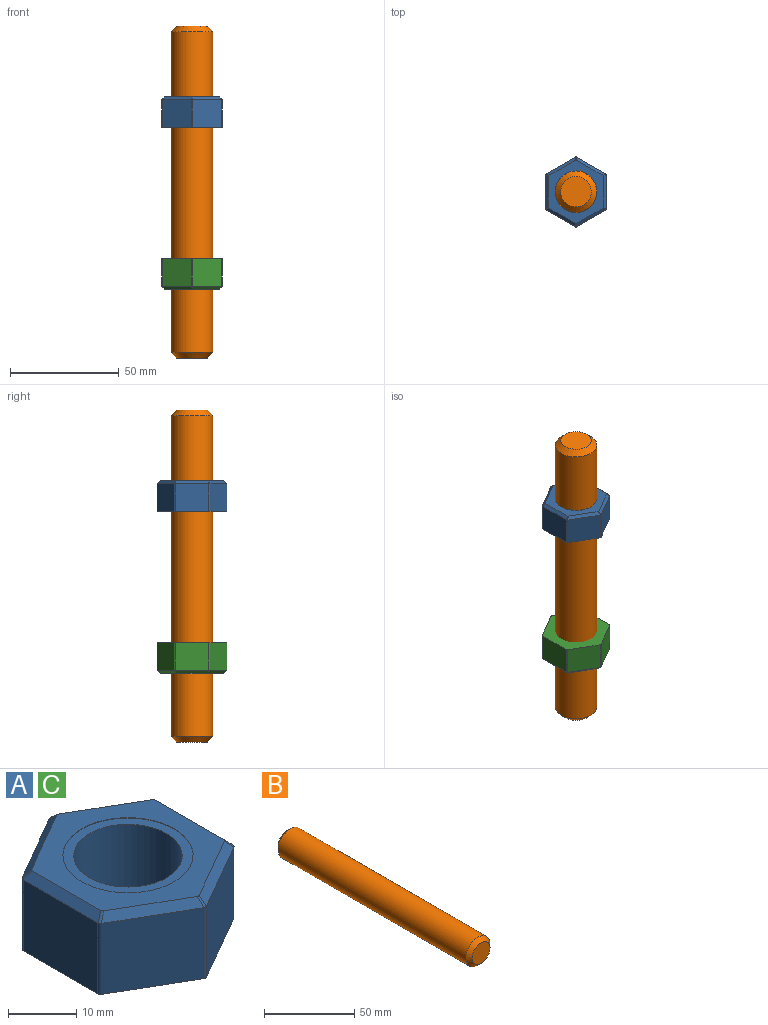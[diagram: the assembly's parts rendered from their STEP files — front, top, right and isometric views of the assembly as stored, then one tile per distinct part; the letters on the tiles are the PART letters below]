
ASSEMBLY  parts=3 mates=1
PART A: 29 faces, bbox 27.9x32.1x14 mm
  f0: plane 19.05x19.05mm, normal (0,0,1), area 87.1mm2, adj f2,f9
  f1: plane 32.05x27.93mm, normal (0,0,-1), area 477.5mm2, adj f2,f3,f4,f5,f6,f7,f8,f18
  f2: cylinder r=7.94mm len=15.88mm, axis (0,0,-1), area 692.8mm2, adj f0,f1
  f3: plane 15.39x12.7mm, normal (1,0,0), area 195.5mm2, adj f1,f14,f18,f26
  f4: plane 13.33x12.7mm, normal (0.5,-0.87,0), area 195.5mm2, adj f1,f12,f18,f20
  f5: plane 13.33x12.7mm, normal (-0.5,-0.87,0), area 195.5mm2, adj f1,f11,f20,f22
  f6: plane 15.39x12.7mm, normal (-1,0,0), area 195.5mm2, adj f1,f13,f22,f24
  f7: plane 13.33x12.7mm, normal (-0.5,0.87,0), area 195.5mm2, adj f1,f15,f24,f28
  f8: plane 13.33x12.7mm, normal (0.5,0.87,0), area 195.5mm2, adj f1,f16,f26,f28
  f9: cylinder r=9.53mm len=19.05mm, axis (0,0,-1), area 4.8mm2, adj f0,f10
  f10: plane 29.18x25.39mm, normal (0,0,1), area 273.2mm2, adj f9,f11,f12,f13,f14,f15,f16,f17
  f11: plane 13.51x8.53mm, normal (-0.35,-0.61,0.71), area 26.7mm2, adj f5,f10,f19,f20,f21,f22
  f12: plane 13.51x8.53mm, normal (0.35,-0.61,0.71), area 26.7mm2, adj f4,f10,f17,f18,f19,f20
  f13: plane 15.6x1.27mm, normal (-0.71,0,0.71), area 26.7mm2, adj f6,f10,f21,f22,f23,f24
  f14: plane 15.6x1.27mm, normal (0.71,0,0.71), area 26.7mm2, adj f3,f10,f17,f18,f25,f26
  f15: plane 13.51x8.53mm, normal (-0.35,0.61,0.71), area 26.7mm2, adj f7,f10,f23,f24,f27,f28
  f16: plane 13.51x8.53mm, normal (0.35,0.61,0.71), area 26.7mm2, adj f8,f10,f25,f26,f27,f28
  f17: cylinder r=0.64mm len=1.5mm, axis (0.65,-0.38,-0.65), area 0.9mm2, adj f10,f12,f14,f18
  f18: cylinder r=0.64mm len=12.73mm, axis (0,0,-1), area 8.5mm2, adj f1,f3,f4,f12,f14,f17
  f19: cylinder r=0.64mm len=1.5mm, axis (0,-0.76,-0.65), area 0.9mm2, adj f10,f11,f12,f20
  f20: cylinder r=0.64mm len=12.73mm, axis (0,0,-1), area 8.5mm2, adj f1,f4,f5,f11,f12,f19
  f21: cylinder r=0.64mm len=1.5mm, axis (0.65,0.38,0.65), area 0.9mm2, adj f10,f11,f13,f22
  f22: cylinder r=0.64mm len=12.73mm, axis (0,0,-1), area 8.5mm2, adj f1,f5,f6,f11,f13,f21
  f23: cylinder r=0.64mm len=1.5mm, axis (0.65,-0.38,0.65), area 0.9mm2, adj f10,f13,f15,f24
  f24: cylinder r=0.64mm len=12.73mm, axis (0,0,-1), area 8.5mm2, adj f1,f6,f7,f13,f15,f23
  f25: cylinder r=0.64mm len=1.5mm, axis (0.65,0.38,-0.65), area 0.9mm2, adj f10,f14,f16,f26
  f26: cylinder r=0.64mm len=12.73mm, axis (0,0,-1), area 8.5mm2, adj f1,f3,f8,f14,f16,f25
  f27: cylinder r=0.64mm len=1.5mm, axis (0,-0.76,0.65), area 0.9mm2, adj f10,f15,f16,f28
  f28: cylinder r=0.64mm len=12.73mm, axis (0,0,-1), area 8.5mm2, adj f1,f7,f8,f15,f16,f27
PART B: 5 faces, bbox 19.1x152.4x19.1 mm
  f0: cylinder r=9.53mm len=147.32mm, axis (0,1,0), area 8816.7mm2, adj f3,f4
  f1: plane 13.97x13.97mm, normal (0,-1,0), area 153.3mm2, adj f4
  f2: plane 13.97x13.97mm, normal (0,1,0), area 153.3mm2, adj f3
  f3: cone r=9.53mm half-angle=45deg, axis (0,-1,0), area 186.3mm2, adj f0,f2
  f4: cone r=6.99mm half-angle=45deg, axis (0,1,0), area 186.3mm2, adj f0,f1
PART C: same geometry as A
PLACE A t=(54.84,34.73,16.7)mm
PLACE B rot(axis=(1,0,0),90deg) t=(54.84,34.73,63.27)mm
PLACE C rot(axis=(1,0,0),180deg) t=(54.84,34.73,-43.49)mm
MATE fastened C.f2 <-> A.f2  axis (0,0,1) through (54.84,34.73,-43.49)mm
